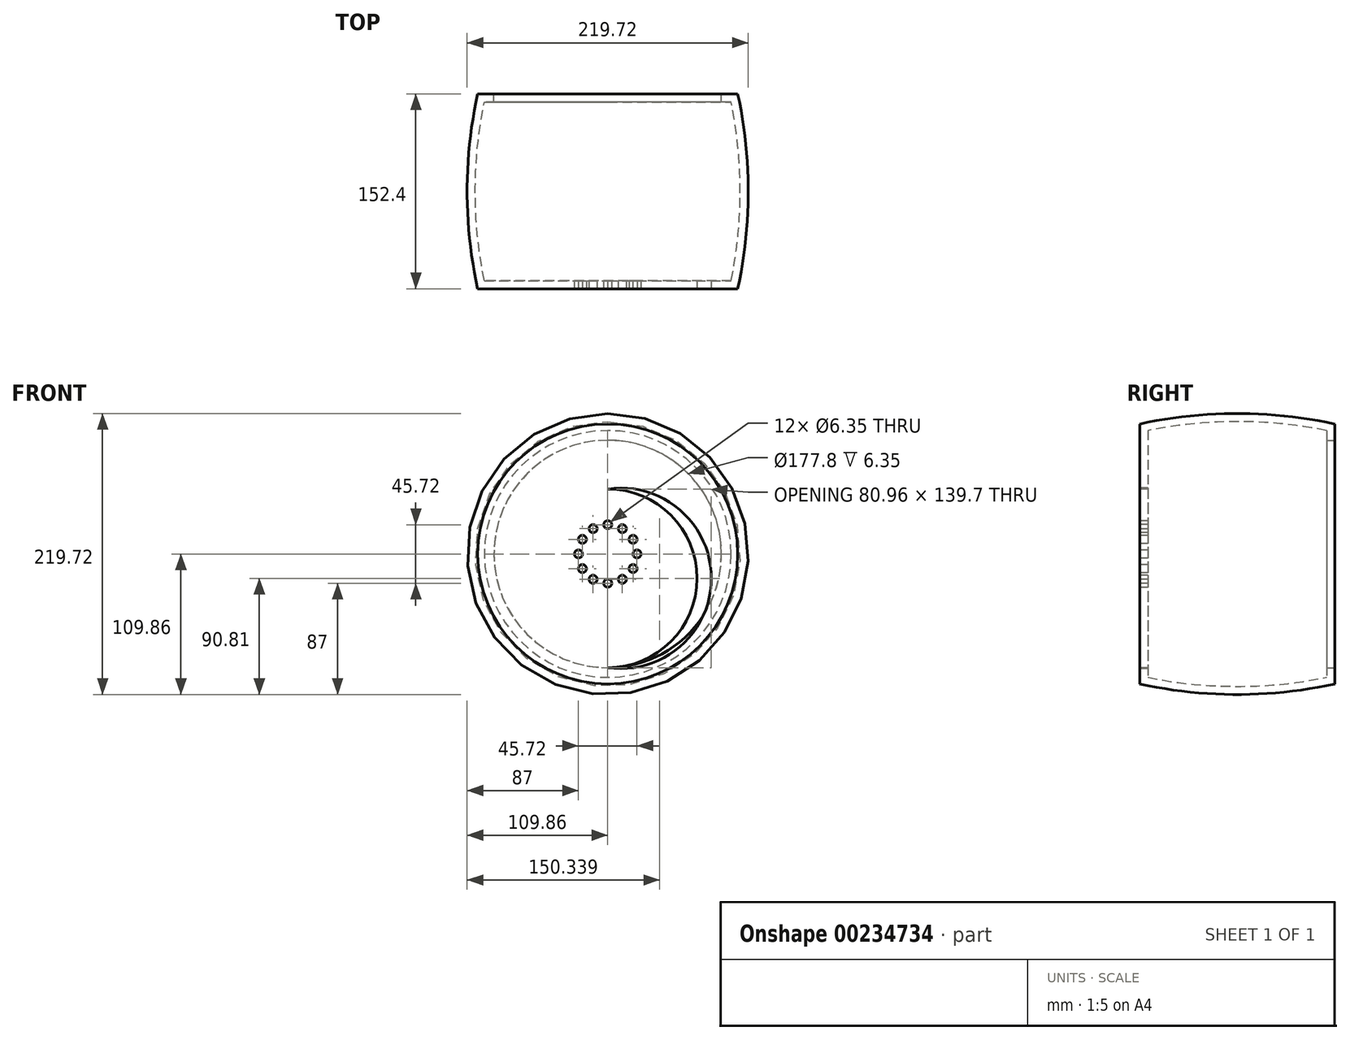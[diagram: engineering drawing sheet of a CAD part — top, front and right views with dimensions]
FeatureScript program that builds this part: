
annotation { "Feature Type Name" : "Feature", "Feature Type Description" : "" }
export const myFeature = defineFeature(function(context is Context, id is Id, definition is map)
    precondition{}
    {
        {
            var Q0;
            Q0=qCreatedBy(makeId("Right.planeOp"),FACE);
            var sketch = newSketch(context, id + "F0", { "sketchPlane" : qUnion([Q0])});
            skLineSegment(sketch, "E0", {"start": v(-76.2, 0) * mm, "end": v(-76.2, 101.6) * mm});
            skLineSegment(sketch, "E1", {"start": v(-69.85, 0) * mm, "end": v(-69.85, 96.45) * mm});
            skArc(sketch, "E2", {"start": v(-76.2, 101.6) * mm, "mid": v(0, 109.86) * mm, "end": v(76.2, 101.6) * mm});
            skArc(sketch, "E3", {"start": v(-69.85, 96.45) * mm, "mid": v(0, 103.51) * mm, "end": v(69.85, 96.45) * mm});
            skLineSegment(sketch, "E4", {"start": v(76.2, 101.6) * mm, "end": v(76.2, 88.9) * mm});
            skLineSegment(sketch, "E5", {"start": v(76.2, 88.9) * mm, "end": v(69.85, 88.9) * mm});
            skLineSegment(sketch, "E6", {"start": v(69.85, 96.45) * mm, "end": v(69.85, 88.9) * mm});
            skLineSegment(sketch, "E7", {"start": v(-69.85, 0) * mm, "end": v(-76.2, 0) * mm});
            skSolve(sketch);
        }
        {
            var Q0;
            Q0=qCreatedBy(makeId("Right.planeOp"),FACE);
            var sketch = newSketch(context, id + "F1", { "sketchPlane" : qUnion([Q0])});
            skLineSegment(sketch, "E8", {"start": v(0, 0) * mm, "end": v(-91.4, 0) * mm, "construction": true});
            skSolve(sketch);
        }
        {
            var Q0;
            Q0 = qSketchRegion(id + "F0", true);
            var Q1;
            Q1=sQuery(id+"F1.wireOp",EDGE,"E8");
            revolve(context, id + "F2", {"entities" : qUnion([Q0]), "axis" : qUnion([Q1]), "revolveType" : RevolveType.FULL});
        }
        {
            var Q0;
            Q0=makeQuery(id+"F2.opRevolve","SWEPT_FACE",FACE,{"disambiguationData":[OSD([sQuery(id+"F0.wireOp",EDGE,"E0")])]});
            var sketch = newSketch(context, id + "F3", { "sketchPlane" : qUnion([Q0])});
            skCircle(sketch, "E9", {"center": v(0, 0) * mm, "radius": 50.8 * mm, "construction": true});
            skCircle(sketch, "E10", {"center": v(0, 0) * mm, "radius": 88.9 * mm, "construction": true});
            skPoint(sketch, "E11.start.orphan", {"position": v(0, 50.8) * mm});
            skArc(sketch, "E12", {"start": v(0, 50.8) * mm, "mid": v(69.85, -19.05) * mm, "end": v(0, -88.9) * mm});
            skArc(sketch, "E13", {"start": v(0, 50.8) * mm, "mid": v(80.96, -19.05) * mm, "end": v(0, -88.9) * mm});
            skSolve(sketch);
        }
        {
            var Q0;
            Q0 = qSketchRegion(id + "F3", true);
            extrude(context, id + "F4", {"entities" : qUnion([Q0]), "operationType" : NewBodyOperationType.REMOVE, "oppositeDirection" : true, "depth" : 25.4 * mm});
        }
        {
            var Q0;
            Q0=makeQuery(id+"F2.opRevolve","SWEPT_FACE",FACE,{"disambiguationData":[OSD([sQuery(id+"F0.wireOp",EDGE,"E0")])]});
            var sketch = newSketch(context, id + "F5", { "sketchPlane" : qUnion([Q0])});
            skCircle(sketch, "E14", {"center": v(0, 0) * mm, "radius": 22.86 * mm, "construction": true});
            skCircle(sketch, "E15", {"center": v(0, 22.86) * mm, "radius": 3.18 * mm});
            skCircle(sketch, "E16.1.0", {"center": v(-11.43, 19.8) * mm, "radius": 3.18 * mm});
            skCircle(sketch, "E16.2.0", {"center": v(-19.8, 11.43) * mm, "radius": 3.18 * mm});
            skCircle(sketch, "E16.3.0", {"center": v(-22.86, 0) * mm, "radius": 3.18 * mm});
            skCircle(sketch, "E16.4.0", {"center": v(-19.8, -11.43) * mm, "radius": 3.18 * mm});
            skCircle(sketch, "E16.5.0", {"center": v(-11.43, -19.8) * mm, "radius": 3.18 * mm});
            skCircle(sketch, "E16.6.0", {"center": v(0, -22.86) * mm, "radius": 3.18 * mm});
            skCircle(sketch, "E16.7.0", {"center": v(11.43, -19.8) * mm, "radius": 3.18 * mm});
            skCircle(sketch, "E16.8.0", {"center": v(19.8, -11.43) * mm, "radius": 3.18 * mm});
            skCircle(sketch, "E16.9.0", {"center": v(22.86, 0) * mm, "radius": 3.18 * mm});
            skCircle(sketch, "E16.10.0", {"center": v(19.8, 11.43) * mm, "radius": 3.18 * mm});
            skCircle(sketch, "E16.11.0", {"center": v(11.43, 19.8) * mm, "radius": 3.18 * mm});
            skSolve(sketch);
        }
        {
            var Q0;
            Q0 = qSketchRegion(id + "F5", true);
            extrude(context, id + "F6", {"entities" : qUnion([Q0]), "operationType" : NewBodyOperationType.REMOVE, "endBound" : BoundingType.THROUGH_ALL, "oppositeDirection" : true, "depth" : 25.4 * mm});
        }
    });
